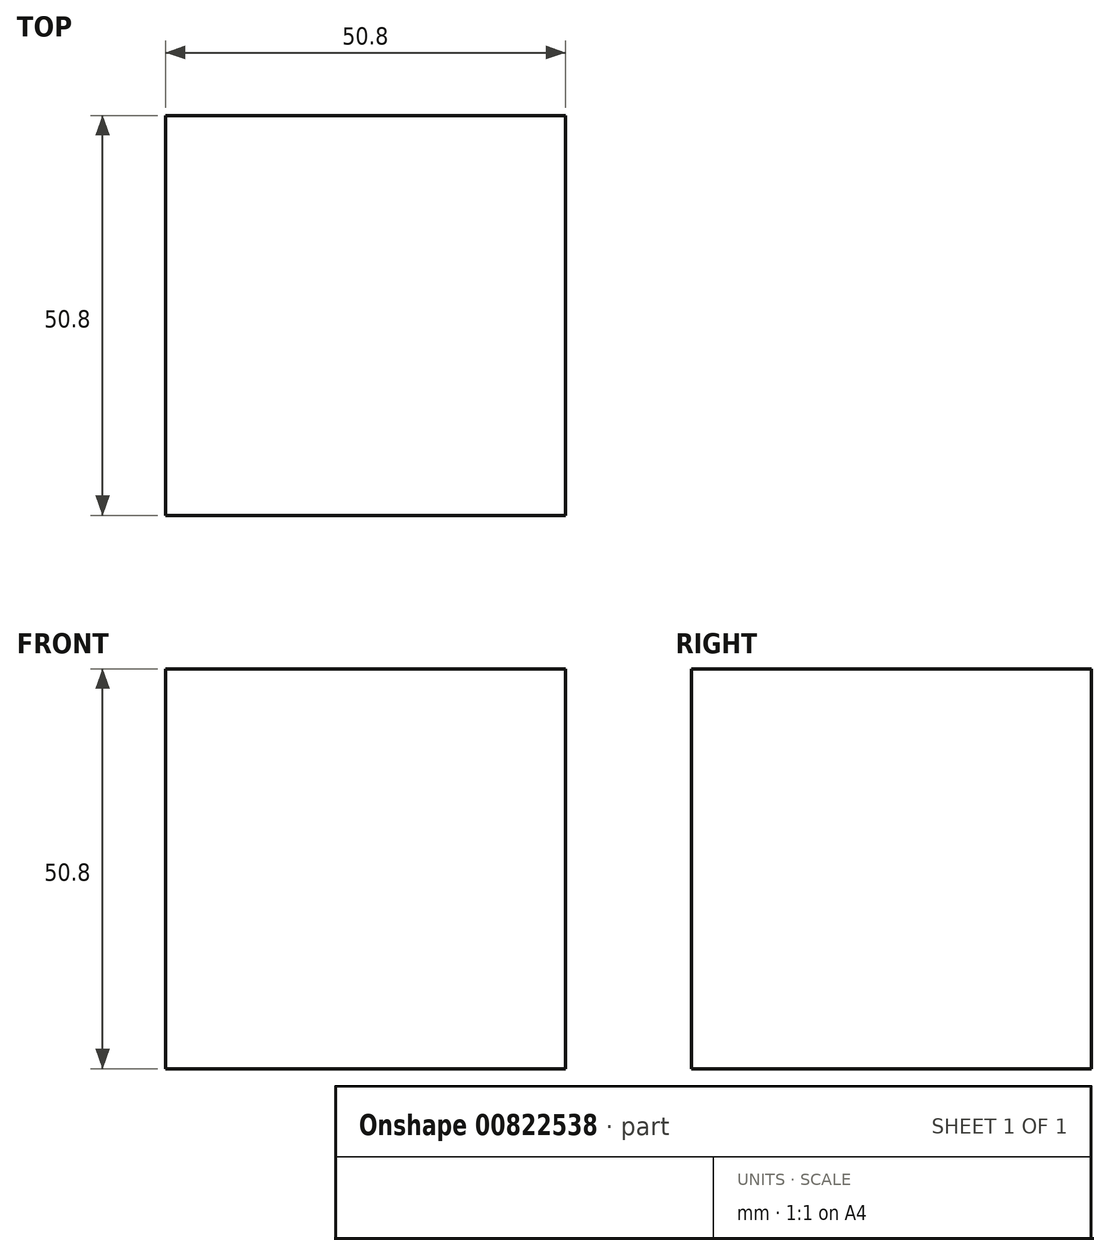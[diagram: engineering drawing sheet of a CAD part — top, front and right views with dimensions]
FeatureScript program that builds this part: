
annotation { "Feature Type Name" : "Feature", "Feature Type Description" : "" }
export const myFeature = defineFeature(function(context is Context, id is Id, definition is map)
    precondition{}
    {
        {
            var Q0;
            Q0=qCreatedBy(makeId("Top.planeOp"),FACE);
            var sketch = newSketch(context, id + "F0", { "sketchPlane" : qUnion([Q0])});
            skLineSegment(sketch, "E0.bottom", {"start": v(25.4, 25.4) * mm, "end": v(-25.4, 25.4) * mm});
            skLineSegment(sketch, "E0.top", {"start": v(25.4, -25.4) * mm, "end": v(-25.4, -25.4) * mm});
            skLineSegment(sketch, "E0.left", {"start": v(25.4, 25.4) * mm, "end": v(25.4, -25.4) * mm});
            skLineSegment(sketch, "E0.right", {"start": v(-25.4, 25.4) * mm, "end": v(-25.4, -25.4) * mm});
            skPoint(sketch, "E0.middle", {"position": v(0, 0) * mm});
            skSolve(sketch);
        }
        {
            var Q0;
            Q0 = qSketchRegion(id + "F0", true);
            extrude(context, id + "F1", {"entities" : qUnion([Q0]), "endBound" : BoundingType.SYMMETRIC, "oppositeDirection" : true, "depth" : 50.8 * mm, "offsetDistance" : 25.4 * mm});
        }
    });
